# Revit family: Construction_Stairs-Precision_Ladders-Alternating_Tread_Ladder_Crossover1
name_source: partatom
category: Specialty Equipment
units: mm (PartAtom-declared; Revit-internal decimal feet)

## family parameters
Always vertical = Yes
Cut with Voids When Loaded = No
OmniClass Number = 23.30.70.17.17
OmniClass Title = Ships Ladders
Part Type = Normal
Room Calculation Point = No
Round Connector Dimension = Use Diameter
Shared = No
Work Plane-Based = No

## types (2) — shared parameters
Default Elevation = 0' - 0"
Description = Alternating Tread Stairs (alternating tread ladders) for rooftop access, mezzanine access, or crossover obstacles
Desired Riser Height = 0' - 8 1/2"
Manufacturer = Precision Ladders, LLC
Material = Metal - Precision Ladders LLC - Aluminum - Mill Finish
Model = Alternating Tread Stairs
Model Number = AT-3
Product Page URL = https://precisionladders.com
Product data url = https://www.bimobject.com
URL = http://www.precisionladders.com

## per-type parameters (varying)
| type | Crossover |
| Crossover | Yes |
| Walk-thru with platform | No |

## geometry (parser evidence)
native form markers: Blend x4, Sweep x9
no freeform markers — native parametric forms only
